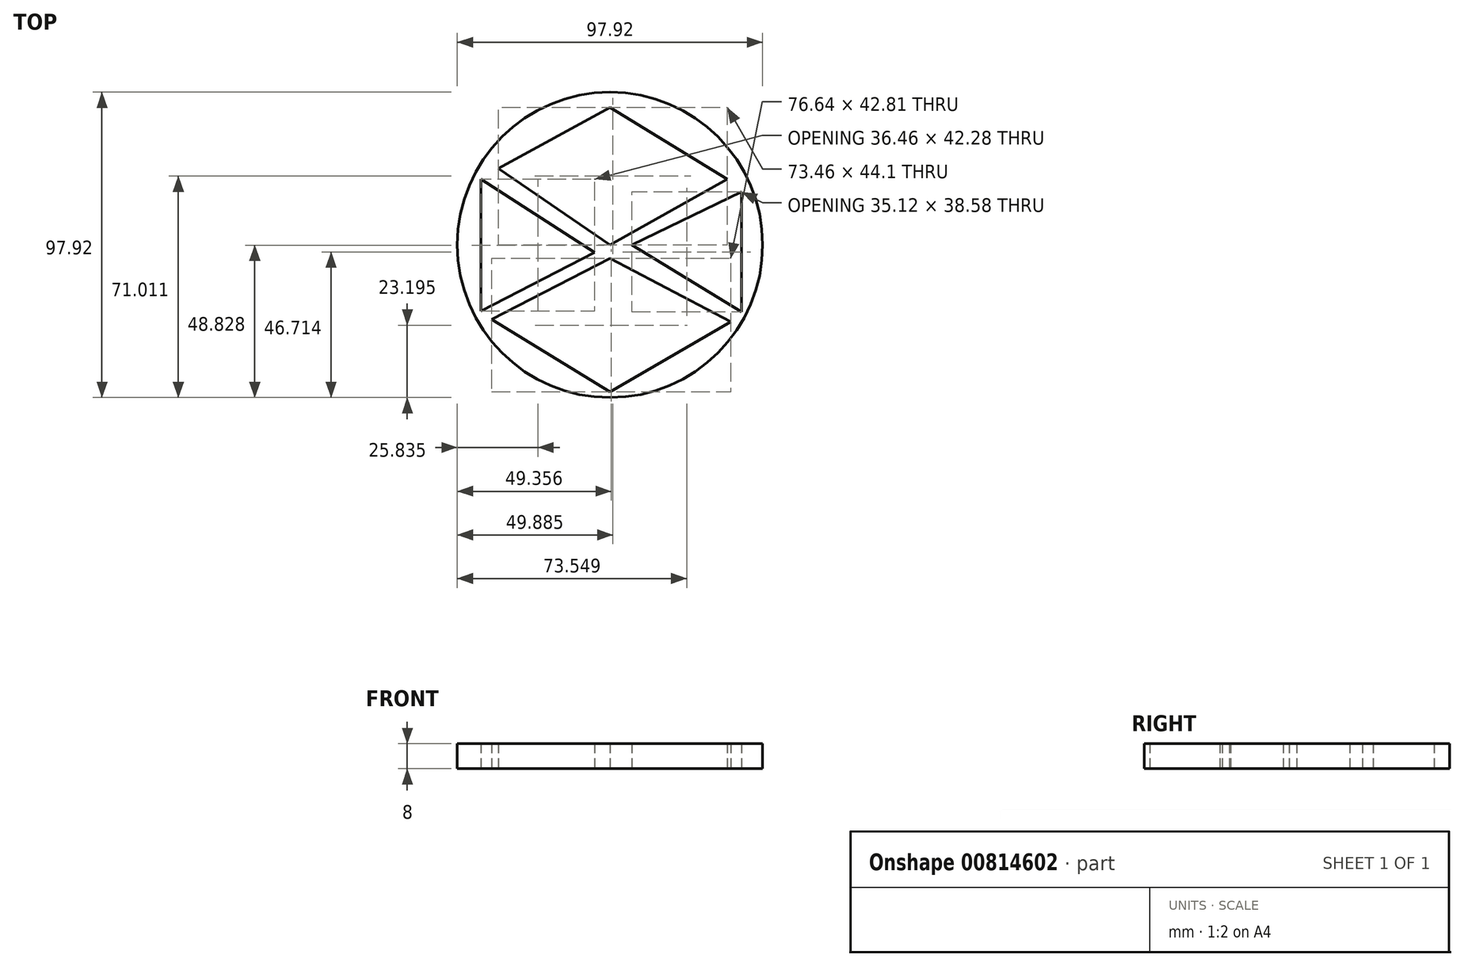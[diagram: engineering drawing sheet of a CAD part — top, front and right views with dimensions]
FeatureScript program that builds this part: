
annotation { "Feature Type Name" : "Feature", "Feature Type Description" : "" }
export const myFeature = defineFeature(function(context is Context, id is Id, definition is map)
    precondition{}
    {
        {
            var Q0;
            Q0=qCreatedBy(makeId("Top.planeOp"),FACE);
            var sketch = newSketch(context, id + "F0", { "sketchPlane" : qUnion([Q0])});
            skLineSegment(sketch, "E0", {"start": v(-37.92, -23.92) * mm, "end": v(0, -47.17) * mm});
            skLineSegment(sketch, "E1", {"start": v(0, -47.17) * mm, "end": v(38.71, -24.7) * mm});
            skLineSegment(sketch, "E2", {"start": v(38.71, -24.7) * mm, "end": v(0, -4.36) * mm});
            skLineSegment(sketch, "E3", {"start": v(0, -4.36) * mm, "end": v(-37.92, -23.92) * mm});
            skLineSegment(sketch, "E4", {"start": v(-41.36, 21) * mm, "end": v(-41.36, -21.27) * mm});
            skLineSegment(sketch, "E5", {"start": v(-41.36, -21.27) * mm, "end": v(-4.9, -2.47) * mm});
            skLineSegment(sketch, "E6", {"start": v(-4.9, -2.47) * mm, "end": v(-41.36, 21) * mm});
            skLineSegment(sketch, "E7", {"start": v(-35.8, 24.44) * mm, "end": v(0, 0) * mm});
            skLineSegment(sketch, "E8", {"start": v(0, 0) * mm, "end": v(37.66, 21) * mm});
            skLineSegment(sketch, "E9", {"start": v(37.66, 21) * mm, "end": v(0, 44.1) * mm});
            skLineSegment(sketch, "E10", {"start": v(0, 44.1) * mm, "end": v(-35.8, 24.44) * mm});
            skLineSegment(sketch, "E11", {"start": v(42.15, 17.04) * mm, "end": v(42.15, -21.54) * mm});
            skLineSegment(sketch, "E12", {"start": v(42.15, -21.54) * mm, "end": v(7.03, 0) * mm});
            skLineSegment(sketch, "E13", {"start": v(7.03, 0) * mm, "end": v(42.15, 17.04) * mm});
            skCircle(sketch, "E14", {"center": v(0, 0) * mm, "radius": 48.96 * mm});
            skSolve(sketch);
        }
        {
            var Q0;
            Q0 = qSketchRegion(id + "F0", true);
            extrude(context, id + "F1", {"entities" : qUnion([Q0]), "depth" : 8 * mm, "offsetDistance" : 25 * mm});
        }
    });
